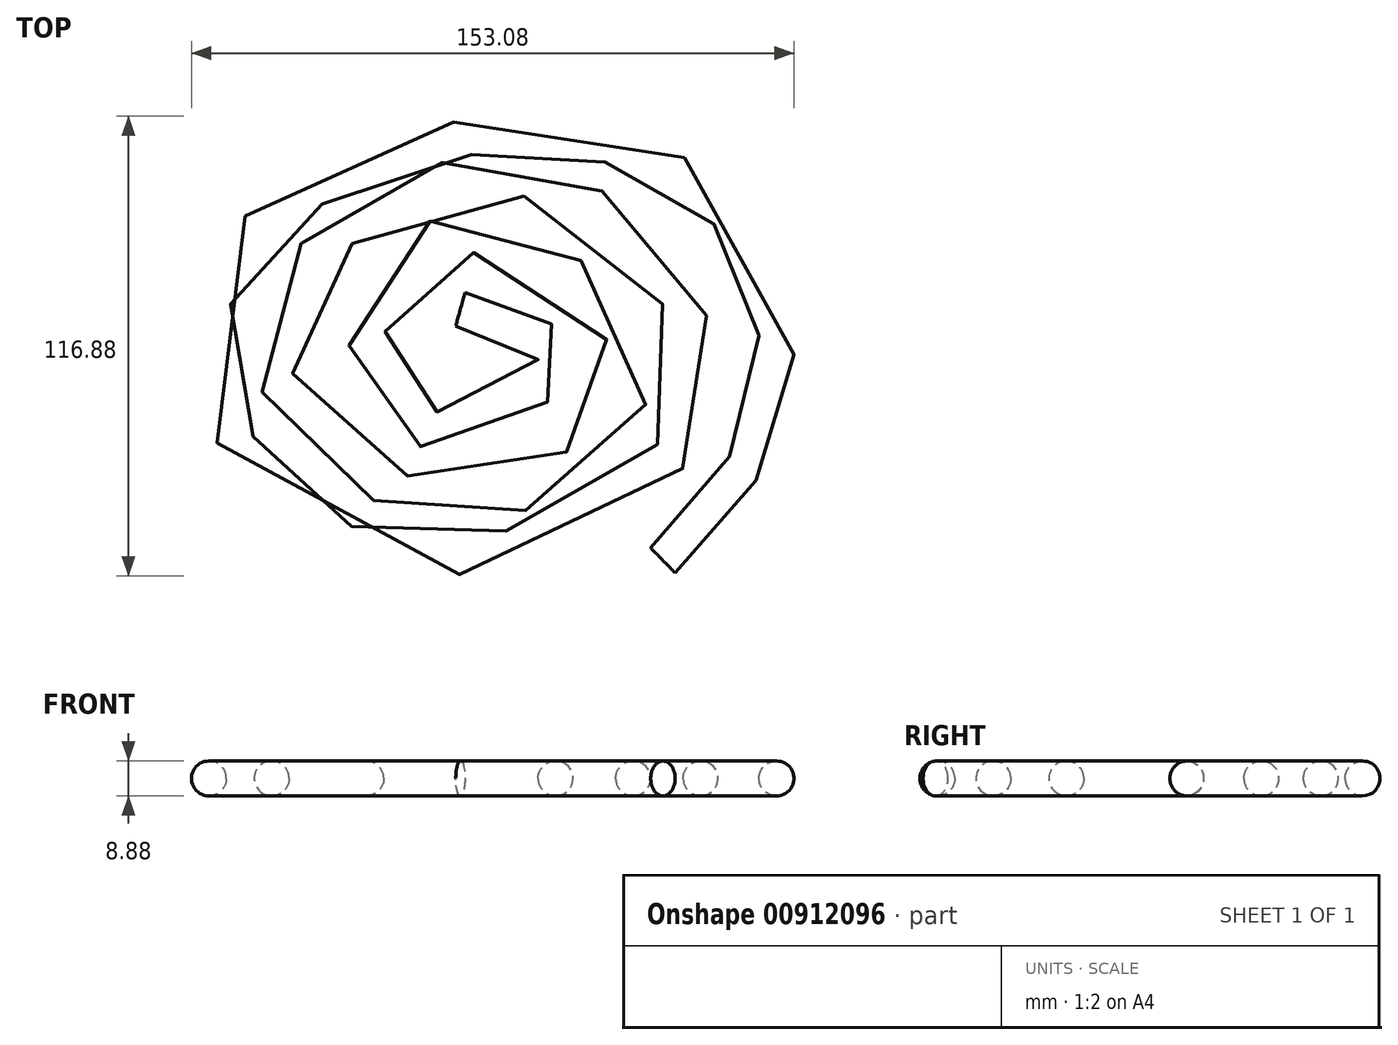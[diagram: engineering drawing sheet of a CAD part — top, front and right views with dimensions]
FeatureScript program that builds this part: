
annotation { "Feature Type Name" : "Feature", "Feature Type Description" : "" }
export const myFeature = defineFeature(function(context is Context, id is Id, definition is map)
    precondition{}
    {
        {
            var Q0;
            Q0=qCreatedBy(makeId("Top.planeOp"),FACE);
            var sketch = newSketch(context, id + "F0", { "sketchPlane" : qUnion([Q0])});
            skFitSpline(sketch, "E0", {"points": [v(44.78, -51.46) * mm, v(69.03, -20.15) * mm, v(69.03, 24.54) * mm, v(35.8, 51.65) * mm, v(-15.18, 52.8) * mm, v(-66.36, 19.76) * mm, v(-57, -30.27) * mm, v(-7.35, -50.5) * mm, v(53.75, -10.03) * mm, v(6.2, 45.16) * mm, v(-53.56, 2.58) * mm, v(-3.72, -36.57) * mm, v(36.57, 0) * mm, v(-16.7, 27.78) * mm, v(-22.25, -15.94) * mm, v(17.1, -2.2) * mm, v(-6.4, 11.36) * mm], "startDerivative": vector(535.72, 521.02) * mm, "endDerivative": vector(-868.2, 238.37) * mm});
            skSolve(sketch);
        }
        {
            var Q0;
            Q0=sQuery(id+"F0.wireOp",VERTEX,"E0.start");
            var Q1;
            Q1=sQuery(id+"F0.wireOp",EDGE,"E0");
            cPlane(context, id + "F1", {"entities" : qUnion([Q0, Q1]), "cplaneType" : CPlaneType.CURVE_POINT, "offset" : 25.4 * mm, "width" : 152.4 * mm, "height" : 152.4 * mm});
        }
        {
            var Q0;
            Q0=qCreatedBy(id+"F1.planeOp",FACE);
            var sketch = newSketch(context, id + "F2", { "sketchPlane" : qUnion([Q0])});
            skCircle(sketch, "E1", {"center": v(-68.72, 0) * mm, "radius": 4.44 * mm});
            skSolve(sketch);
        }
        {
            var Q0;
            Q0 = qSketchRegion(id + "F2", true);
            var Q1;
            Q1 = qConstructionFilter(qBodyType(qCreatedBy(id + "F0" ,EDGE), BodyType.WIRE), ConstructionObject.NO);
            sweep(context, id + "F3", {"profiles" : qUnion([Q0]), "path" : qUnion([Q1])});
        }
    });
